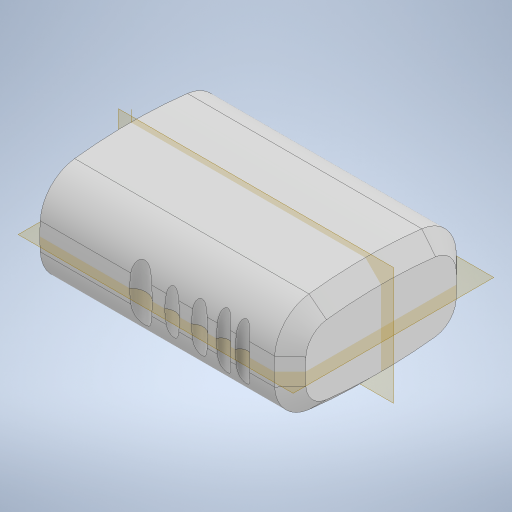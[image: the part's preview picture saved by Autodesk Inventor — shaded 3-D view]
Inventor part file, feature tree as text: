
AUTODESK INVENTOR PART (.ipt)
format: ipt  version: 2023 (Build 270158030, 158C)  size: 420,352 bytes
history: native  units: mm
features: extrude x3, sketch x3, fillet x2, chamfer x2, mirror x1, projected_geometry x1
ambient origin geometry x8: Origin, YZ Plane, XZ Plane, XY Plane, X Axis, Y Axis, Z Axis, Center Point
bodies: Solid1 (feature_tree)
feature tree (12):
  extrude  "Extrusion1"  Depth=30.0mm
  extrude  "Extrusion2"  Depth=30.0mm
  fillet  "Fillet1"  Radius=9.4mm
  chamfer  "Chamfer1"  Distance=1.3mm
  fillet  "Fillet3"  Radius=30.0mm
  chamfer  "Chamfer2"  Distance=2.0mm
  extrude  "Extrusion3"  Depth=10.0mm
  mirror  "Mirror1"
  sketch  "Sketch1"  dims[d0=60.0mm d1=30.0mm]
  sketch  "Sketch2"  dims[d2=60.0mm d3=30.0mm d4=9.4mm]
  projected_geometry  "Projected Loop1"
  sketch  "Sketch3"  dims[d5=20.0mm d6=1.3mm d7=30.0mm d8=0.0mm d9=2.0mm d10=0.0mm d11=5.0mm d13=2.0mm d14=2.0mm d15=45.0deg d16=3.0mm d17=1.0mm d18=2.0mm d19=45.0deg d20=4.7mm d21=10.0mm d22=3.0mm d23=2.0mm d24=2.0mm d25=2.0mm d26=-0.349066mm d27=3.0mm d28=4.0mm d29=0.4mm d30=1.1mm d31=1.2mm d32=1.4mm]
